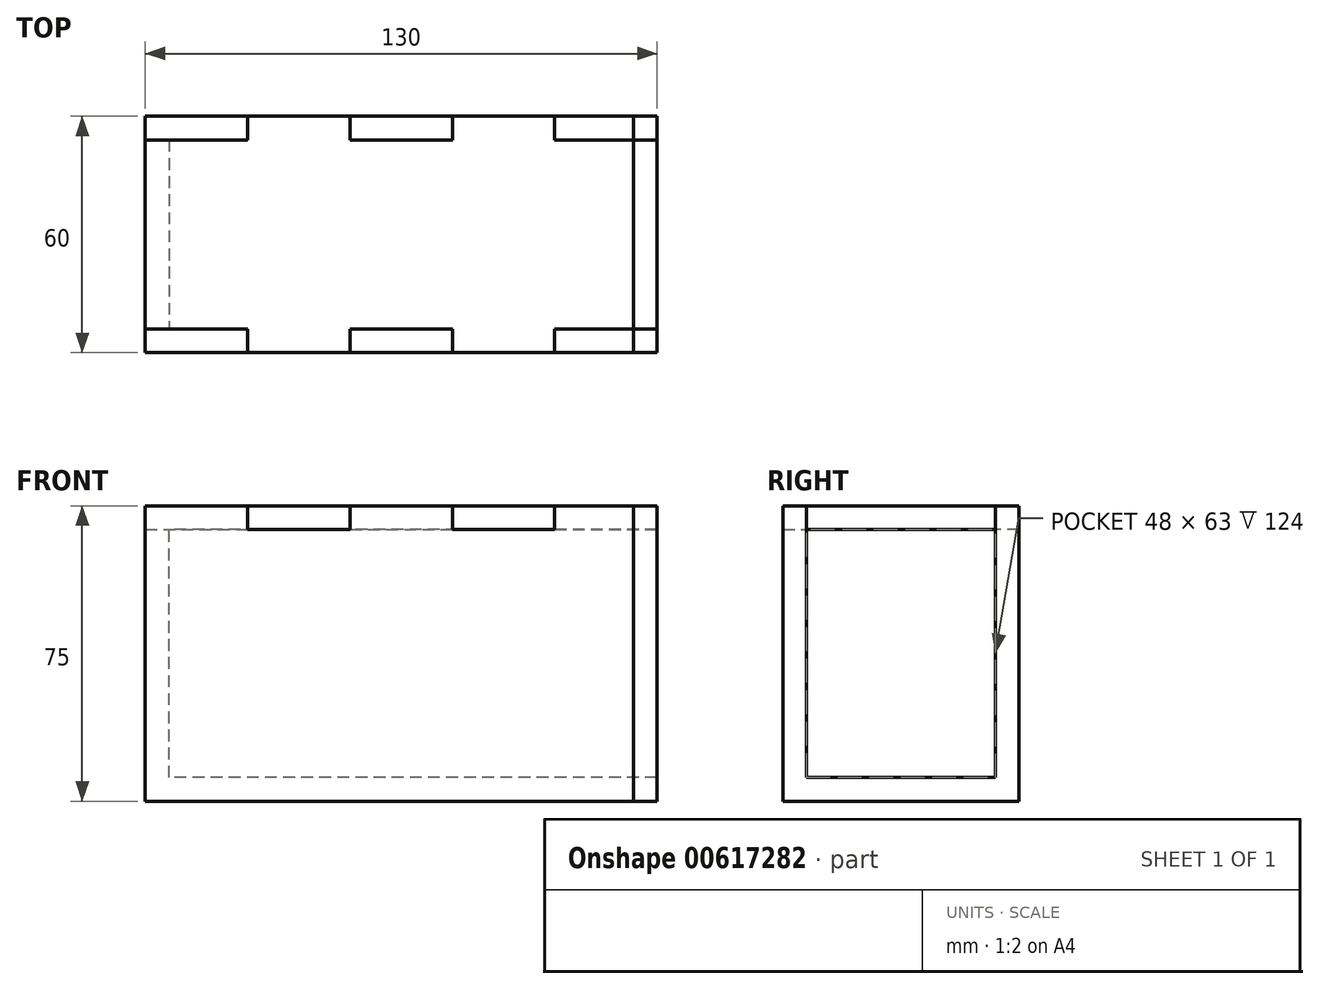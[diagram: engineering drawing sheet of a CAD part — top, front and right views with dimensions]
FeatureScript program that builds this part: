
annotation { "Feature Type Name" : "Feature", "Feature Type Description" : "" }
export const myFeature = defineFeature(function(context is Context, id is Id, definition is map)
    precondition{}
    {
        {
            var Q0;
            Q0=qCreatedBy(makeId("Right.planeOp"),FACE);
            var sketch = newSketch(context, id + "F0", { "sketchPlane" : qUnion([Q0])});
            skLineSegment(sketch, "E0.bottom", {"start": v(22.72, 0) * mm, "end": v(-37.28, 0) * mm});
            skLineSegment(sketch, "E0.top", {"start": v(22.72, 75) * mm, "end": v(-37.28, 75) * mm});
            skLineSegment(sketch, "E0.left", {"start": v(22.72, 0) * mm, "end": v(22.72, 75) * mm});
            skLineSegment(sketch, "E0.right", {"start": v(-37.28, 0) * mm, "end": v(-37.28, 75) * mm});
            skSolve(sketch);
        }
        {
            var Q0;
            Q0=makeQuery(id+"F0.imprint","IMPRINT",FACE,{"disambiguationData":[TD([[makeQuery(id+"F0.imprint","IMPRINT",EDGE,{"derivedFrom":sQuery(id+"F0.wireOp",EDGE,"E0.bottom")}),-1.0]])]});
            extrude(context, id + "F1", {"entities" : qUnion([Q0]), "depth" : 65 * mm, "offsetDistance" : 25 * mm});
        }
        {
            var Q0;
            Q0=makeQuery(id+"F1.opExtrude","CAP_FACE",FACE,{"disambiguationData":[OSD([sQuery(id+"F0.wireOp",EDGE,"E0.bottom"),sQuery(id+"F0.wireOp",EDGE,"E0.top"),sQuery(id+"F0.wireOp",EDGE,"E0.left"),sQuery(id+"F0.wireOp",EDGE,"E0.right")])],"isStart":true});
            extrude(context, id + "F2", {"entities" : qUnion([Q0]), "operationType" : NewBodyOperationType.ADD, "depth" : 65 * mm, "offsetDistance" : 25 * mm});
        }
        {
            var Q0;
            Q0=makeQuery(id+"F1.opExtrude","CAP_FACE",FACE,{"disambiguationData":[OSD([sQuery(id+"F0.wireOp",EDGE,"E0.bottom"),sQuery(id+"F0.wireOp",EDGE,"E0.top"),sQuery(id+"F0.wireOp",EDGE,"E0.left"),sQuery(id+"F0.wireOp",EDGE,"E0.right")])],"isStart":false});
            shell(context, id + "F3", {"entities" : qUnion([Q0]), "thickness" : 6 * mm});
        }
        {
            var Q0;
            {var subQ0=sQuery(id+"F0.wireOp",EDGE,"E0.top");Q0=makeQuery(id+"F2.boolean.opBoolean","MERGE",FACE,{"derivedFrom":[makeQuery(id+"F1.opExtrude","SWEPT_FACE",FACE,{"disambiguationData":[OSD([subQ0])]}),makeQuery(id+"F2.opExtrude","SWEPT_FACE",FACE,{"disambiguationData":[OSD([subQ0])]})]});}
            var sketch = newSketch(context, id + "F4", { "sketchPlane" : qUnion([Q0])});
            skLineSegment(sketch, "E1.bottom", {"start": v(-65, 22.72) * mm, "end": v(-39, 22.72) * mm});
            skLineSegment(sketch, "E1.top", {"start": v(-65, 16.72) * mm, "end": v(-39, 16.72) * mm});
            skLineSegment(sketch, "E1.left", {"start": v(-65, 22.72) * mm, "end": v(-65, 16.72) * mm});
            skLineSegment(sketch, "E1.right", {"start": v(-39, 22.72) * mm, "end": v(-39, 16.72) * mm});
            skLineSegment(sketch, "E2.1.0.0", {"start": v(-13, 22.72) * mm, "end": v(-13, 16.72) * mm});
            skLineSegment(sketch, "E2.2.0.0", {"start": v(13, 22.72) * mm, "end": v(13, 16.72) * mm});
            skLineSegment(sketch, "E2.2.0.1", {"start": v(-13, 16.72) * mm, "end": v(13, 16.72) * mm});
            skLineSegment(sketch, "E3.direction1", {"start": v(-13, 16.72) * mm, "end": v(13, 16.72) * mm, "construction": true});
            skLineSegment(sketch, "E4.3.1.0", {"start": v(39, 22.72) * mm, "end": v(39, 16.72) * mm});
            skLineSegment(sketch, "E4.0.2.0", {"start": v(39, 16.72) * mm, "end": v(65, 16.72) * mm});
            skLineSegment(sketch, "E4.3.2.0", {"start": v(65, 22.72) * mm, "end": v(65, 16.72) * mm});
            skLineSegment(sketch, "E5.bottom", {"start": v(-65, -37.28) * mm, "end": v(-39, -37.28) * mm});
            skLineSegment(sketch, "E5.top", {"start": v(-65, -31.28) * mm, "end": v(-39, -31.28) * mm});
            skLineSegment(sketch, "E5.left", {"start": v(-65, -37.28) * mm, "end": v(-65, -31.28) * mm});
            skLineSegment(sketch, "E5.right", {"start": v(-39, -37.28) * mm, "end": v(-39, -31.28) * mm});
            skLineSegment(sketch, "E6.1.0.1", {"start": v(-13, -37.28) * mm, "end": v(-13, -31.28) * mm});
            skLineSegment(sketch, "E6.2.0.0", {"start": v(-13, -31.28) * mm, "end": v(13, -31.28) * mm});
            skLineSegment(sketch, "E6.2.0.1", {"start": v(13, -37.28) * mm, "end": v(13, -31.28) * mm});
            skLineSegment(sketch, "E6.direction1", {"start": v(-65, -31.28) * mm, "end": v(-39, -31.28) * mm, "construction": true});
            skLineSegment(sketch, "E7.3.3.0", {"start": v(39, -37.28) * mm, "end": v(39, -31.28) * mm});
            skLineSegment(sketch, "E7.0.4.0", {"start": v(39, -31.28) * mm, "end": v(65, -31.28) * mm});
            skLineSegment(sketch, "E7.3.4.0", {"start": v(65, -37.28) * mm, "end": v(65, -31.28) * mm});
            skSolve(sketch);
        }
        {
            var Q0;
            {var subQ9=sQuery(id+"F4.wireOp",EDGE,"E1.top");Q0=makeQuery(id+"F4.imprint","IMPRINT",FACE,{"disambiguationData":[TD([[makeQuery(id+"F4.imprint","IMPRINT",EDGE,{"derivedFrom":subQ9}),-1.0]])]});}
            extrude(context, id + "F5", {"entities" : qUnion([Q0]), "oppositeDirection" : true, "depth" : 6 * mm, "offsetDistance" : 25 * mm});
        }
        {
            var Q0;
            Q0=makeQuery(id+"F1.opExtrude","CAP_FACE",FACE,{"disambiguationData":[OSD([sQuery(id+"F0.wireOp",EDGE,"E0.bottom"),sQuery(id+"F0.wireOp",EDGE,"E0.top"),sQuery(id+"F0.wireOp",EDGE,"E0.left"),sQuery(id+"F0.wireOp",EDGE,"E0.right")])],"isStart":false});
            var sketch = newSketch(context, id + "F6", { "sketchPlane" : qUnion([Q0])});
            skLineSegment(sketch, "E8.bottom", {"start": v(-37.28, 75) * mm, "end": v(22.72, 75) * mm});
            skLineSegment(sketch, "E8.top", {"start": v(-37.28, 0) * mm, "end": v(22.72, 0) * mm});
            skLineSegment(sketch, "E8.left", {"start": v(-37.28, 75) * mm, "end": v(-37.28, 0) * mm});
            skLineSegment(sketch, "E8.right", {"start": v(22.72, 75) * mm, "end": v(22.72, 0) * mm});
            skSolve(sketch);
        }
        {
            var Q0;
            Q0 = qSketchRegion(id + "F6", true);
            extrude(context, id + "F7", {"entities" : qUnion([Q0]), "oppositeDirection" : true, "depth" : 6 * mm, "offsetDistance" : 25 * mm});
        }
    });
